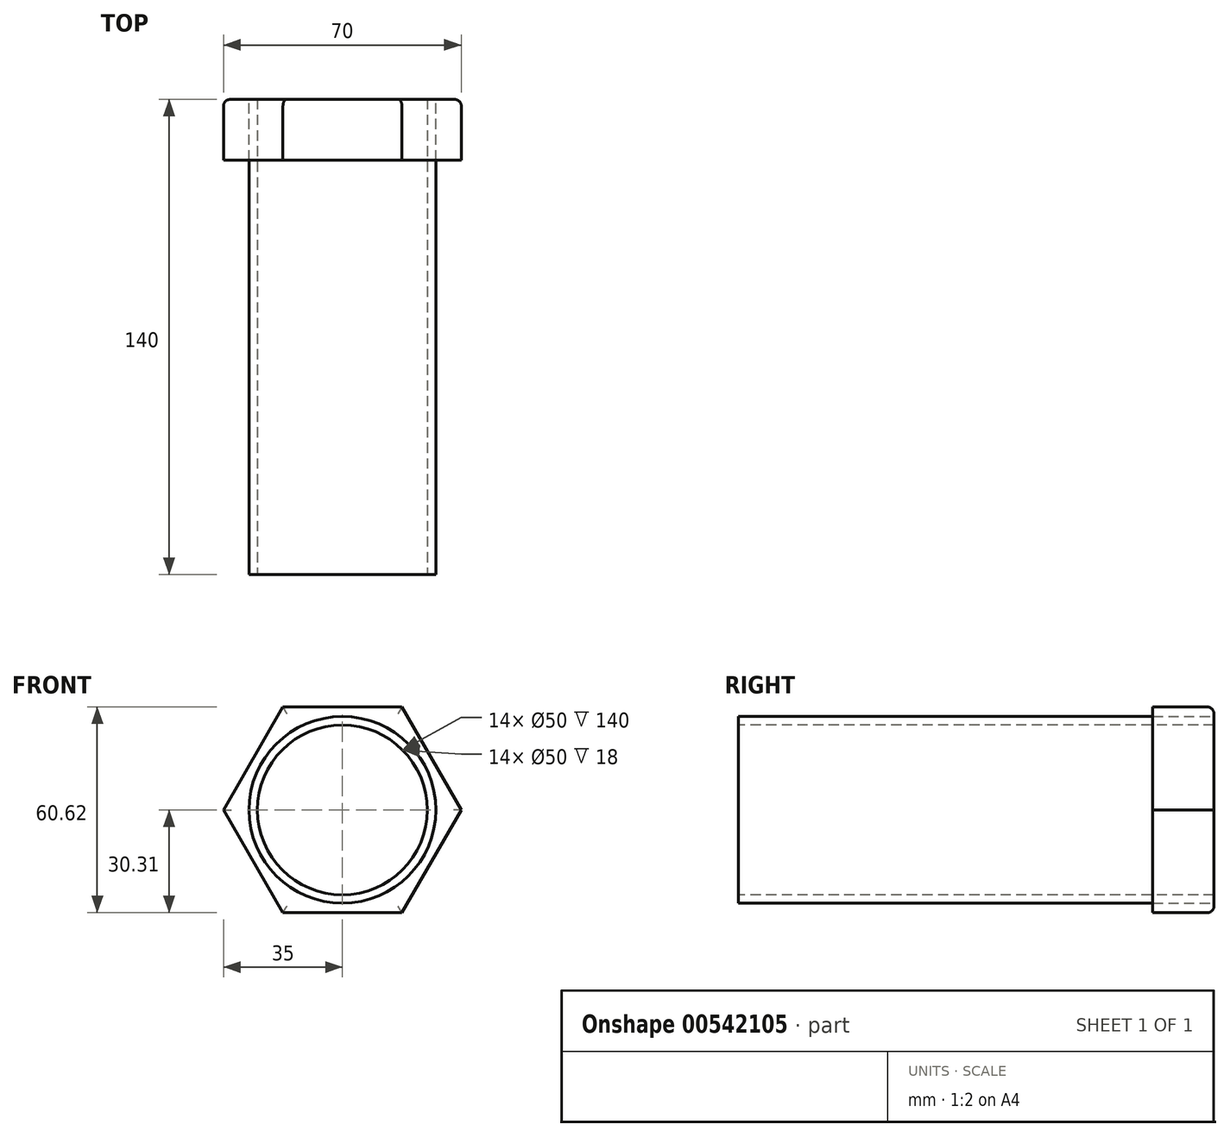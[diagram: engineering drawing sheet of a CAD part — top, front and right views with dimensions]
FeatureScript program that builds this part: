
annotation { "Feature Type Name" : "Feature", "Feature Type Description" : "" }
export const myFeature = defineFeature(function(context is Context, id is Id, definition is map)
    precondition{}
    {
        {
            var Q0;
            Q0=qCreatedBy(makeId("Front.planeOp"),FACE);
            var sketch = newSketch(context, id + "F0", { "sketchPlane" : qUnion([Q0])});
            skCircle(sketch, "E0.cCircle", {"center": v(0, 0) * mm, "radius": 30.31 * mm, "construction": true});
            skLineSegment(sketch, "E0.0", {"start": v(17.5, -30.31) * mm, "end": v(-17.5, -30.31) * mm});
            skLineSegment(sketch, "E0.1", {"start": v(-17.5, -30.31) * mm, "end": v(-35, 0) * mm});
            skLineSegment(sketch, "E0.2", {"start": v(-35, 0) * mm, "end": v(-17.5, 30.31) * mm});
            skLineSegment(sketch, "E0.3", {"start": v(-17.5, 30.31) * mm, "end": v(17.5, 30.31) * mm});
            skLineSegment(sketch, "E0.4", {"start": v(17.5, 30.31) * mm, "end": v(35, 0) * mm});
            skLineSegment(sketch, "E0.5", {"start": v(35, 0) * mm, "end": v(17.5, -30.31) * mm});
            skPoint(sketch, "E0.0.midPoint", {"position": v(0, -30.31) * mm});
            skSolve(sketch);
        }
        {
            var Q0;
            Q0=makeQuery(id+"F0.imprint","IMPRINT",FACE,{"disambiguationData":[TD([[makeQuery(id+"F0.imprint","IMPRINT",EDGE,{"derivedFrom":sQuery(id+"F0.wireOp",EDGE,"E0.0")}),-1.0]])]});
            var sketch = newSketch(context, id + "F1", { "sketchPlane" : qUnion([Q0])});
            skCircle(sketch, "E1", {"center": v(0, 0) * mm, "radius": 27.5 * mm});
            skSolve(sketch);
        }
        {
            var Q0;
            Q0=makeQuery(id+"F0.imprint","IMPRINT",FACE,{"disambiguationData":[TD([[makeQuery(id+"F0.imprint","IMPRINT",EDGE,{"derivedFrom":sQuery(id+"F0.wireOp",EDGE,"E0.0")}),-1.0]])]});
            extrude(context, id + "F2", {"entities" : qUnion([Q0]), "depth" : 18 * mm, "offsetDistance" : 25 * mm});
        }
        {
            var Q0;
            Q0 = qSketchRegion(id + "F1", true);
            var Q1;
            Q1=sQuery(id+"F1.wireOp",EDGE,"E1");
            extrude(context, id + "F3", {"bodyType" : ToolBodyType.SURFACE, "operationType" : NewBodyOperationType.ADD, "surfaceEntities" : qUnion([Q0, Q1]), "depth" : 140 * mm, "offsetDistance" : 25 * mm});
        }
        {
            var Q0;
            Q0=makeQuery(id+"F3.opExtrude","CAP_FACE",FACE,{"disambiguationData":[OSD([sQuery(id+"F1.wireOp",EDGE,"E1")])],"isStart":false});
            var sketch = newSketch(context, id + "F4", { "sketchPlane" : qUnion([Q0])});
            skCircle(sketch, "E2", {"center": v(0, 0) * mm, "radius": 25 * mm});
            skSolve(sketch);
        }
        {
            var Q0;
            Q0 = qSketchRegion(id + "F4", true);
            var Q1;
            Q1=makeQuery(id+"F4.imprint","IMPRINT",FACE,{"disambiguationData":[TD([[makeQuery(id+"F4.imprint","IMPRINT",EDGE,{"derivedFrom":sQuery(id+"F4.wireOp",EDGE,"E2")}),1.0]])]});
            extrude(context, id + "F5", {"entities" : qUnion([Q0, Q1]), "operationType" : NewBodyOperationType.REMOVE, "oppositeDirection" : true, "depth" : 140 * mm, "offsetDistance" : 25 * mm});
        }
        {
            var Q0;
            Q0=makeQuery(id+"F2.opExtrude","CAP_EDGE",EDGE,{"disambiguationData":[OSD([sQuery(id+"F0.wireOp",EDGE,"E0.5")])],"isStart":true});
            var Q1;
            Q1=makeQuery(id+"F2.opExtrude","CAP_EDGE",EDGE,{"disambiguationData":[OSD([sQuery(id+"F0.wireOp",EDGE,"E0.4")])],"isStart":true});
            var Q2;
            Q2=makeQuery(id+"F2.opExtrude","CAP_EDGE",EDGE,{"disambiguationData":[OSD([sQuery(id+"F0.wireOp",EDGE,"E0.3")])],"isStart":true});
            var Q3;
            Q3=makeQuery(id+"F2.opExtrude","CAP_EDGE",EDGE,{"disambiguationData":[OSD([sQuery(id+"F0.wireOp",EDGE,"E0.2")])],"isStart":true});
            var Q4;
            Q4=makeQuery(id+"F2.opExtrude","CAP_EDGE",EDGE,{"disambiguationData":[OSD([sQuery(id+"F0.wireOp",EDGE,"E0.1")])],"isStart":true});
            var Q5;
            Q5=makeQuery(id+"F2.opExtrude","CAP_EDGE",EDGE,{"disambiguationData":[OSD([sQuery(id+"F0.wireOp",EDGE,"E0.0")])],"isStart":true});
            fillet(context, id + "F6", {"entities" : qUnion([Q0, Q1, Q2, Q3, Q4, Q5]), "radius" : 2 * mm, "tangentPropagation" : true, "allowEdgeOverflow" : false});
        }
    });
